# Revit family: Accessory-Back_Splash -KOHLER-Quartz-K-36572-1
name_source: partatom
category: Specialty Equipment
units: mm (PartAtom-declared; Revit-internal decimal feet)

## family parameters
Cut with Voids When Loaded = No
Host = Face
OmniClass Number = 23.21.19.15
OmniClass Title = Specialty Casework
Part Type = Normal
Room Calculation Point = No
Round Connector Dimension = Use Diameter
Shared = No

## types (1)
- MMW-Miami White
    ADA Compliant = No
    Assembly Code = C1030200
    Date Modified = 07/16/2024
    Default Elevation = 42"
    Description = 73 BACKSPLASH (73 CM x 35 CM x 2 CM)
    Finish = KOHLER-Quartz-MMW-Miami_White
    Height = 3 1/2"
    Length = 73 1/8"
    Manufacturer = Kohler Co.
    Master Format 2014 = 10 28 00
    Master Format 2014 Name = Toilet, Bath, and Laundry Accessories
    Material = Quartz
    Model = K-36572-MMW
    Product Documentation Link = https://www.us.kohler.com
    Product Name = Quartz
    Product Page URL = http://www.us.kohler.com
    Type = 1
    URL = https://www.us.kohler.com
    WaterSense Certified = No
    Width = 13/16"

## geometry (parser evidence)
native form markers: Sweep x5
no freeform markers — native parametric forms only
